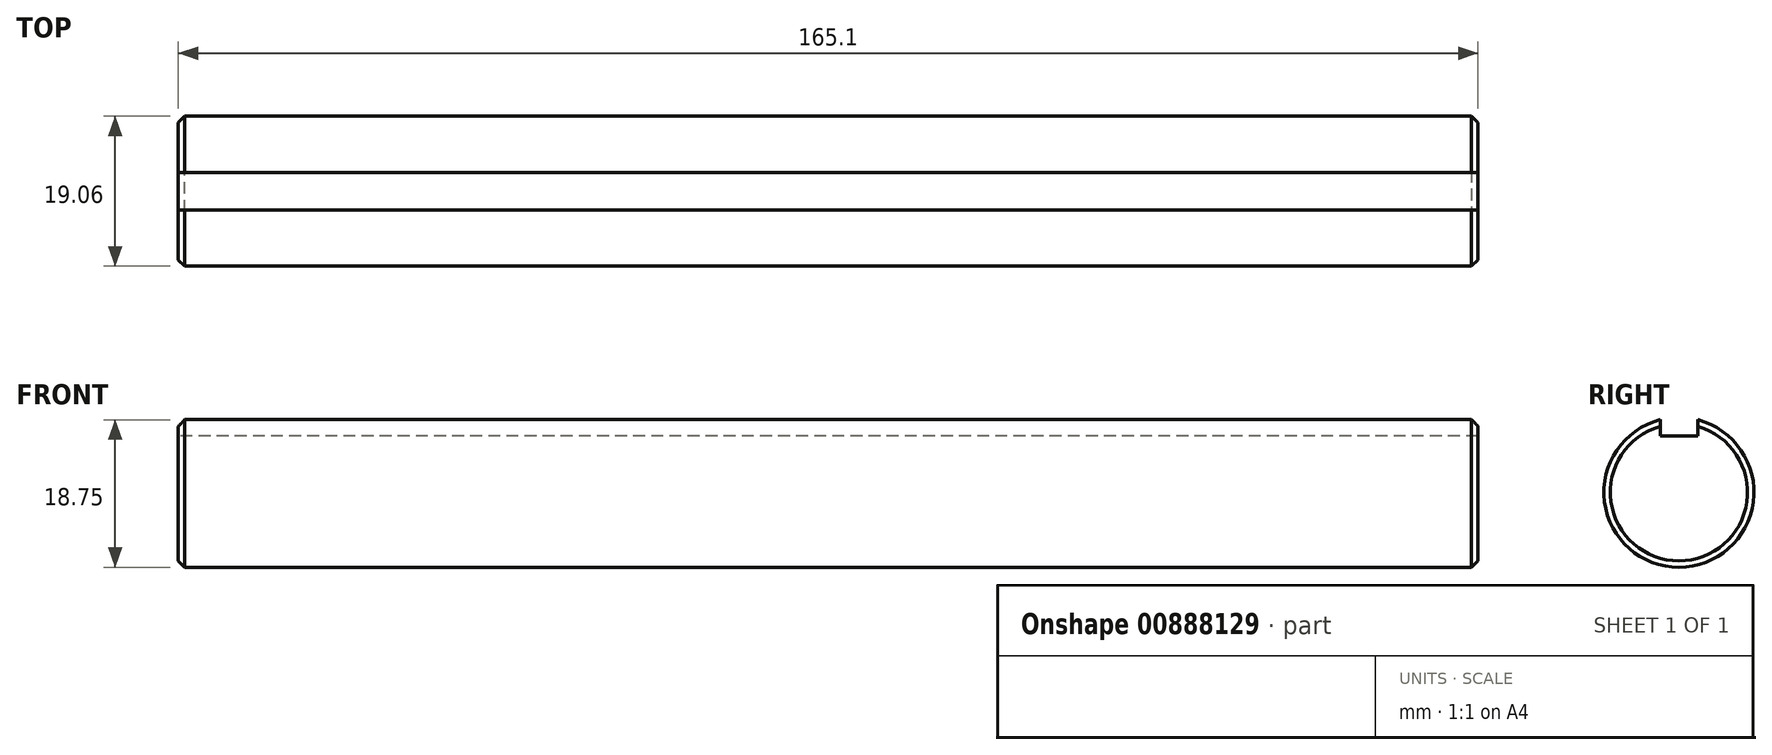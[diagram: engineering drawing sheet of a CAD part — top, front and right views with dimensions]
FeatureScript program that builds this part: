
annotation { "Feature Type Name" : "Feature", "Feature Type Description" : "" }
export const myFeature = defineFeature(function(context is Context, id is Id, definition is map)
    precondition{}
    {
        {
            var Q0;
            Q0=qCreatedBy(makeId("Right.planeOp"),FACE);
            var sketch = newSketch(context, id + "F0", { "sketchPlane" : qUnion([Q0])});
            skArc(sketch, "E0", {"start": v(-2.38, 9.22) * mm, "mid": v(0, -9.53) * mm, "end": v(2.38, 9.22) * mm});
            skLineSegment(sketch, "E1", {"start": v(0, 0) * mm, "end": v(0, 9.53) * mm, "construction": true});
            skLineSegment(sketch, "E2.bottom", {"start": v(2.38, 11.9) * mm, "end": v(-2.38, 11.9) * mm, "construction": true});
            skLineSegment(sketch, "E2.top", {"start": v(2.38, 7.14) * mm, "end": v(-2.38, 7.14) * mm});
            skLineSegment(sketch, "E2.left", {"start": v(2.38, 11.9) * mm, "end": v(2.38, 9.22) * mm, "construction": true});
            skLineSegment(sketch, "E2.right", {"start": v(-2.38, 11.9) * mm, "end": v(-2.38, 9.22) * mm, "construction": true});
            skPoint(sketch, "E2.middle", {"position": v(0, 9.53) * mm});
            skLineSegment(sketch, "E3", {"start": v(-2.38, 9.22) * mm, "end": v(-2.38, 7.14) * mm});
            skLineSegment(sketch, "E4", {"start": v(2.38, 9.22) * mm, "end": v(2.38, 7.14) * mm});
            skSolve(sketch);
        }
        {
            var Q0;
            Q0 = qSketchRegion(id + "F0", true);
            extrude(context, id + "F1", {"entities" : qUnion([Q0]), "depth" : 165.1 * mm, "offsetDistance" : 25.4 * mm, "symmetric" : true});
        }
        {
            var Q0;
            Q0=qCreatedBy(makeId("Front.planeOp"),FACE);
            var sketch = newSketch(context, id + "F2", { "sketchPlane" : qUnion([Q0])});
            skLineSegment(sketch, "E5.0", {"start": v(82.55, 9.22) * mm, "end": v(-82.55, 9.22) * mm, "construction": true});
            skLineSegment(sketch, "E6.0", {"start": v(-82.55, 9.22) * mm, "end": v(-82.55, -9.53) * mm, "construction": true});
            skLineSegment(sketch, "E7", {"start": v(82.55, -9.53) * mm, "end": v(-82.55, -9.53) * mm, "construction": true});
            skLineSegment(sketch, "E8.0", {"start": v(82.55, 9.22) * mm, "end": v(82.55, -9.53) * mm, "construction": true});
            skLineSegment(sketch, "E9", {"start": v(79.76, 11.5) * mm, "end": v(84.84, 6.43) * mm});
            skLineSegment(sketch, "E10", {"start": v(84.84, 6.43) * mm, "end": v(84.84, 11.5) * mm});
            skLineSegment(sketch, "E11", {"start": v(84.84, 11.5) * mm, "end": v(79.76, 11.5) * mm});
            skPoint(sketch, "E12", {"position": v(82.04, 9.22) * mm});
            skPoint(sketch, "E13", {"position": v(82.55, 8.71) * mm});
            skLineSegment(sketch, "E14", {"start": v(82.3, 8.97) * mm, "end": v(84.84, 11.5) * mm, "construction": true});
            skLineSegment(sketch, "E15", {"start": v(0, 0) * mm, "end": v(82.55, 0) * mm, "construction": true});
            skLineSegment(sketch, "E16", {"start": v(0, 0) * mm, "end": v(0, 9.22) * mm, "construction": true});
            skLineSegment(sketch, "E17.MirrorCS", {"start": v(-84.84, 11.5) * mm, "end": v(-79.76, 11.5) * mm});
            skLineSegment(sketch, "E18.MirrorCS", {"start": v(-79.76, 11.5) * mm, "end": v(-84.84, 6.43) * mm});
            skLineSegment(sketch, "E19.MirrorCS", {"start": v(-84.84, 6.43) * mm, "end": v(-84.84, 11.5) * mm});
            skSolve(sketch);
        }
        {
            var Q0;
            Q0 = qSketchRegion(id + "F2", true);
            var Q1;
            Q1=sQuery(id+"F2.wireOp",EDGE,"E15");
            revolve(context, id + "F3", {"operationType" : NewBodyOperationType.REMOVE, "surfaceOperationType" : NewSurfaceOperationType.NEW, "entities" : qUnion([Q0]), "axis" : qUnion([Q1]), "revolveType" : RevolveType.FULL, "oppositeDirection" : true});
        }
    });
